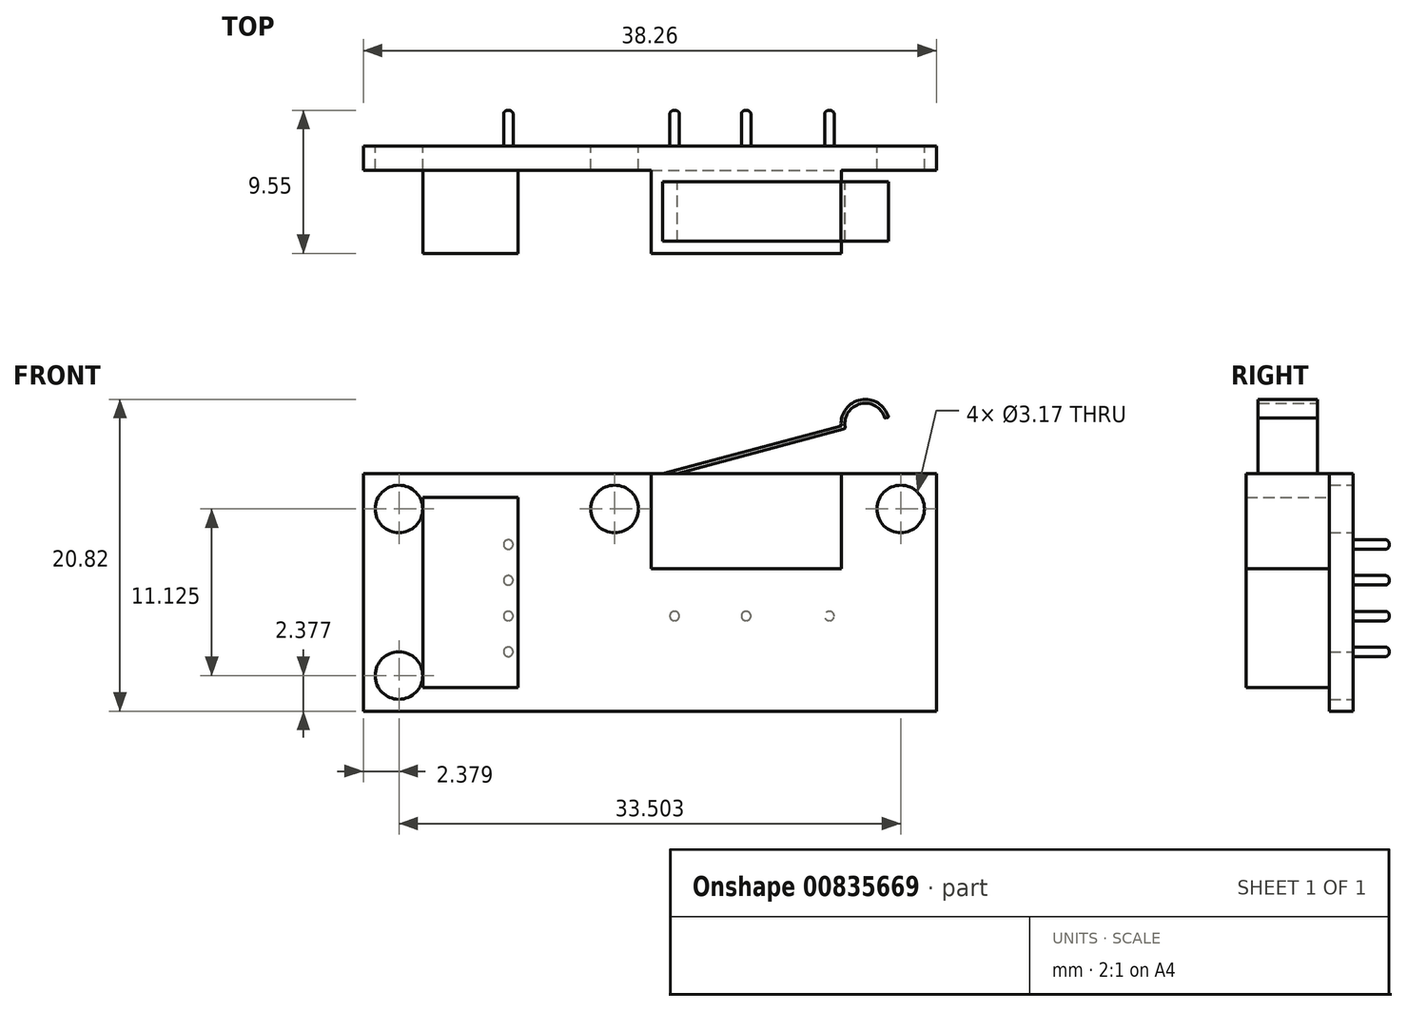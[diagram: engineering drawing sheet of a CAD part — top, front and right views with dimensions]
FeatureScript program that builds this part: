
annotation { "Feature Type Name" : "Feature", "Feature Type Description" : "" }
export const myFeature = defineFeature(function(context is Context, id is Id, definition is map)
    precondition{}
    {
        {
            var Q0;
            Q0=qCreatedBy(makeId("Front.planeOp"),FACE);
            var sketch = newSketch(context, id + "F0", { "sketchPlane" : qUnion([Q0])});
            skLineSegment(sketch, "E0.bottom", {"start": v(-19.13, 7.94) * mm, "end": v(19.13, 7.94) * mm});
            skLineSegment(sketch, "E0.top", {"start": v(-19.13, -7.94) * mm, "end": v(19.13, -7.94) * mm});
            skLineSegment(sketch, "E0.left", {"start": v(-19.13, 7.94) * mm, "end": v(-19.13, -7.94) * mm});
            skLineSegment(sketch, "E0.right", {"start": v(19.13, 7.94) * mm, "end": v(19.13, -7.94) * mm});
            skLineSegment(sketch, "E1", {"start": v(-19.13, -7.94) * mm, "end": v(19.13, 7.94) * mm, "construction": true});
            skSolve(sketch);
        }
        {
            var Q0;
            Q0=makeQuery(id+"F0.imprint","IMPRINT",FACE,{"disambiguationData":[TD([[makeQuery(id+"F0.imprint","IMPRINT",EDGE,{"derivedFrom":sQuery(id+"F0.wireOp",EDGE,"E0.bottom")}),-1.0]])]});
            extrude(context, id + "F1", {"entities" : qUnion([Q0]), "depth" : 1.6 * mm, "offsetDistance" : 25.4 * mm});
        }
        {
            var Q0;
            Q0=makeQuery(id+"F1.opExtrude","CAP_FACE",FACE,{"disambiguationData":[OSD([sQuery(id+"F0.wireOp",EDGE,"E0.bottom"),sQuery(id+"F0.wireOp",EDGE,"E0.top"),sQuery(id+"F0.wireOp",EDGE,"E0.left"),sQuery(id+"F0.wireOp",EDGE,"E0.right")])],"isStart":false});
            var sketch = newSketch(context, id + "F2", { "sketchPlane" : qUnion([Q0])});
            skLineSegment(sketch, "E2.bottom", {"start": v(0.08, 7.94) * mm, "end": v(12.78, 7.94) * mm});
            skLineSegment(sketch, "E2.top", {"start": v(0.08, 1.59) * mm, "end": v(12.78, 1.59) * mm});
            skLineSegment(sketch, "E2.left", {"start": v(0.08, 7.94) * mm, "end": v(0.08, 1.59) * mm});
            skLineSegment(sketch, "E2.right", {"start": v(12.78, 7.94) * mm, "end": v(12.78, 1.59) * mm});
            skLineSegment(sketch, "E3.bottom", {"start": v(-15.16, 6.35) * mm, "end": v(-8.81, 6.35) * mm});
            skLineSegment(sketch, "E3.top", {"start": v(-15.16, -6.35) * mm, "end": v(-8.81, -6.35) * mm});
            skLineSegment(sketch, "E3.left", {"start": v(-15.16, 6.35) * mm, "end": v(-15.16, -6.35) * mm});
            skLineSegment(sketch, "E3.right", {"start": v(-8.81, 6.35) * mm, "end": v(-8.81, -6.35) * mm});
            skSolve(sketch);
        }
        {
            var Q0;
            Q0 = qSketchRegion(id + "F2", true);
            extrude(context, id + "F3", {"entities" : qUnion([Q0]), "operationType" : NewBodyOperationType.ADD, "depth" : 5.56 * mm, "offsetDistance" : 25.4 * mm});
        }
        {
            var Q0;
            Q0=makeQuery(id+"F1.opExtrude","CAP_FACE",FACE,{"disambiguationData":[OSD([sQuery(id+"F0.wireOp",EDGE,"E0.bottom"),sQuery(id+"F0.wireOp",EDGE,"E0.top"),sQuery(id+"F0.wireOp",EDGE,"E0.left"),sQuery(id+"F0.wireOp",EDGE,"E0.right")])],"isStart":false});
            cPlane(context, id + "F4", {"entities" : qUnion([Q0]), "cplaneType" : CPlaneType.OFFSET, "offset" : 0.79 * mm, "width" : 152.4 * mm, "height" : 152.4 * mm});
        }
        {
            var Q0;
            Q0=qCreatedBy(id+"F4.planeOp",FACE);
            var sketch = newSketch(context, id + "F5", { "sketchPlane" : qUnion([Q0])});
            skLineSegment(sketch, "E4", {"start": v(0.86, 7.94) * mm, "end": v(12.78, 11.11) * mm});
            skArc(sketch, "E5", {"start": v(15.84, 11.93) * mm, "mid": v(13.96, 12.82) * mm, "end": v(12.78, 11.11) * mm});
            skLineSegment(sketch, "E6.0", {"start": v(1.85, 7.94) * mm, "end": v(13.07, 10.93) * mm});
            skLineSegment(sketch, "E7", {"start": v(0.86, 7.94) * mm, "end": v(1.85, 7.94) * mm});
            skArc(sketch, "E8", {"start": v(15.68, 11.62) * mm, "mid": v(14.03, 12.58) * mm, "end": v(13.07, 10.93) * mm});
            skArc(sketch, "E9", {"start": v(15.93, 11.7) * mm, "mid": v(15.9, 11.81) * mm, "end": v(15.84, 11.93) * mm});
            skLineSegment(sketch, "E10", {"start": v(15.68, 11.62) * mm, "end": v(15.93, 11.7) * mm});
            skLineSegment(sketch, "E11", {"start": v(12.78, 11.11) * mm, "end": v(15.84, 11.93) * mm, "construction": true});
            skSolve(sketch);
        }
        {
            var Q0;
            Q0 = qSketchRegion(id + "F5", true);
            extrude(context, id + "F6", {"entities" : qUnion([Q0]), "operationType" : NewBodyOperationType.ADD, "depth" : 3.96 * mm, "offsetDistance" : 25.4 * mm});
        }
        {
            var Q0;
            Q0=makeQuery(id+"F6.opExtrude","SWEPT_EDGE",EDGE,{"disambiguationData":[OSD([sQuery(id+"F5.wireOp",EDGE,"E4"),sQuery(id+"F5.wireOp",EDGE,"E5")])]});
            var Q1;
            Q1=makeQuery(id+"F6.opExtrude","SWEPT_EDGE",EDGE,{"disambiguationData":[OSD([sQuery(id+"F5.wireOp",EDGE,"E9"),sQuery(id+"F5.wireOp",EDGE,"E10")])]});
            var Q2;
            Q2=makeQuery(id+"F6.opExtrude","SWEPT_EDGE",EDGE,{"disambiguationData":[OSD([sQuery(id+"F5.wireOp",EDGE,"E8"),sQuery(id+"F5.wireOp",EDGE,"E10")])]});
            fillet(context, id + "F7", {"entities" : qUnion([Q0, Q1, Q2]), "radius" : 0.03 * mm, "tangentPropagation" : true, "allowEdgeOverflow" : false});
        }
        {
            var Q0;
            Q0=makeQuery(id+"F6.opExtrude","SWEPT_EDGE",EDGE,{"disambiguationData":[OSD([sQuery(id+"F5.wireOp",EDGE,"E6.0"),sQuery(id+"F5.wireOp",EDGE,"E8")])]});
            fillet(context, id + "F8", {"entities" : qUnion([Q0]), "radius" : 0.13 * mm, "tangentPropagation" : true, "allowEdgeOverflow" : false});
        }
        {
            var Q0;
            Q0=makeQuery(id+"F1.opExtrude","CAP_FACE",FACE,{"disambiguationData":[OSD([sQuery(id+"F0.wireOp",EDGE,"E0.bottom"),sQuery(id+"F0.wireOp",EDGE,"E0.top"),sQuery(id+"F0.wireOp",EDGE,"E0.left"),sQuery(id+"F0.wireOp",EDGE,"E0.right")])],"isStart":true});
            var sketch = newSketch(context, id + "F9", { "sketchPlane" : qUnion([Q0])});
            skCircle(sketch, "E12", {"center": v(-11.99, -1.59) * mm, "radius": 0.32 * mm});
            skCircle(sketch, "E13", {"center": v(-6.43, -1.59) * mm, "radius": 0.32 * mm});
            skCircle(sketch, "E14", {"center": v(-1.65, -1.59) * mm, "radius": 0.32 * mm});
            skCircle(sketch, "E15", {"center": v(9.45, 0.8) * mm, "radius": 0.32 * mm});
            skCircle(sketch, "E16", {"center": v(9.45, 3.19) * mm, "radius": 0.32 * mm});
            skCircle(sketch, "E17", {"center": v(9.45, -1.59) * mm, "radius": 0.32 * mm});
            skCircle(sketch, "E18", {"center": v(9.45, -3.98) * mm, "radius": 0.32 * mm});
            skSolve(sketch);
        }
        {
            var Q0;
            Q0 = qSketchRegion(id + "F9", true);
            extrude(context, id + "F10", {"entities" : qUnion([Q0]), "operationType" : NewBodyOperationType.ADD, "depth" : 2.4 * mm, "offsetDistance" : 25.4 * mm});
        }
        {
            var Q0;
            Q0=makeQuery(id+"F10.opExtrude","CAP_EDGE",EDGE,{"disambiguationData":[OSD([sQuery(id+"F9.wireOp",EDGE,"E12")])],"isStart":false});
            var Q1;
            Q1=makeQuery(id+"F10.opExtrude","CAP_EDGE",EDGE,{"disambiguationData":[OSD([sQuery(id+"F9.wireOp",EDGE,"E13")])],"isStart":false});
            var Q2;
            Q2=makeQuery(id+"F10.opExtrude","CAP_EDGE",EDGE,{"disambiguationData":[OSD([sQuery(id+"F9.wireOp",EDGE,"E14")])],"isStart":false});
            var Q3;
            Q3=makeQuery(id+"F10.opExtrude","CAP_EDGE",EDGE,{"disambiguationData":[OSD([sQuery(id+"F9.wireOp",EDGE,"E16")])],"isStart":false});
            var Q4;
            Q4=makeQuery(id+"F10.opExtrude","CAP_EDGE",EDGE,{"disambiguationData":[OSD([sQuery(id+"F9.wireOp",EDGE,"E15")])],"isStart":false});
            var Q5;
            Q5=makeQuery(id+"F10.opExtrude","CAP_EDGE",EDGE,{"disambiguationData":[OSD([sQuery(id+"F9.wireOp",EDGE,"E17")])],"isStart":false});
            var Q6;
            Q6=makeQuery(id+"F10.opExtrude","CAP_EDGE",EDGE,{"disambiguationData":[OSD([sQuery(id+"F9.wireOp",EDGE,"E18")])],"isStart":false});
            fillet(context, id + "F11", {"entities" : qUnion([Q0, Q1, Q2, Q3, Q4, Q5, Q6]), "radius" : 0.25 * mm, "tangentPropagation" : true, "allowEdgeOverflow" : false});
        }
        {
            var Q0;
            Q0=makeQuery(id+"F1.opExtrude","CAP_FACE",FACE,{"disambiguationData":[OSD([sQuery(id+"F0.wireOp",EDGE,"E0.bottom"),sQuery(id+"F0.wireOp",EDGE,"E0.top"),sQuery(id+"F0.wireOp",EDGE,"E0.left"),sQuery(id+"F0.wireOp",EDGE,"E0.right")])],"isStart":true});
            var sketch = newSketch(context, id + "F12", { "sketchPlane" : qUnion([Q0])});
            skCircle(sketch, "E19", {"center": v(-16.75, 5.56) * mm, "radius": 1.59 * mm});
            skCircle(sketch, "E20", {"center": v(2.35, 5.56) * mm, "radius": 1.59 * mm});
            skCircle(sketch, "E21", {"center": v(16.75, 5.56) * mm, "radius": 1.59 * mm});
            skCircle(sketch, "E22", {"center": v(16.75, -5.56) * mm, "radius": 1.59 * mm});
            skSolve(sketch);
        }
        {
            var Q0;
            Q0 = qSketchRegion(id + "F12", true);
            var Q1;
            Q1=makeQuery(id+"F1.opExtrude","CAP_FACE",FACE,{"disambiguationData":[OSD([sQuery(id+"F0.wireOp",EDGE,"E0.bottom"),sQuery(id+"F0.wireOp",EDGE,"E0.top"),sQuery(id+"F0.wireOp",EDGE,"E0.left"),sQuery(id+"F0.wireOp",EDGE,"E0.right")])],"isStart":false});
            extrude(context, id + "F13", {"entities" : qUnion([Q0]), "operationType" : NewBodyOperationType.REMOVE, "endBound" : BoundingType.UP_TO_SURFACE, "oppositeDirection" : true, "depth" : 25.4 * mm, "endBoundEntityFace" : qUnion([Q1]), "offsetDistance" : 25.4 * mm});
        }
    });
